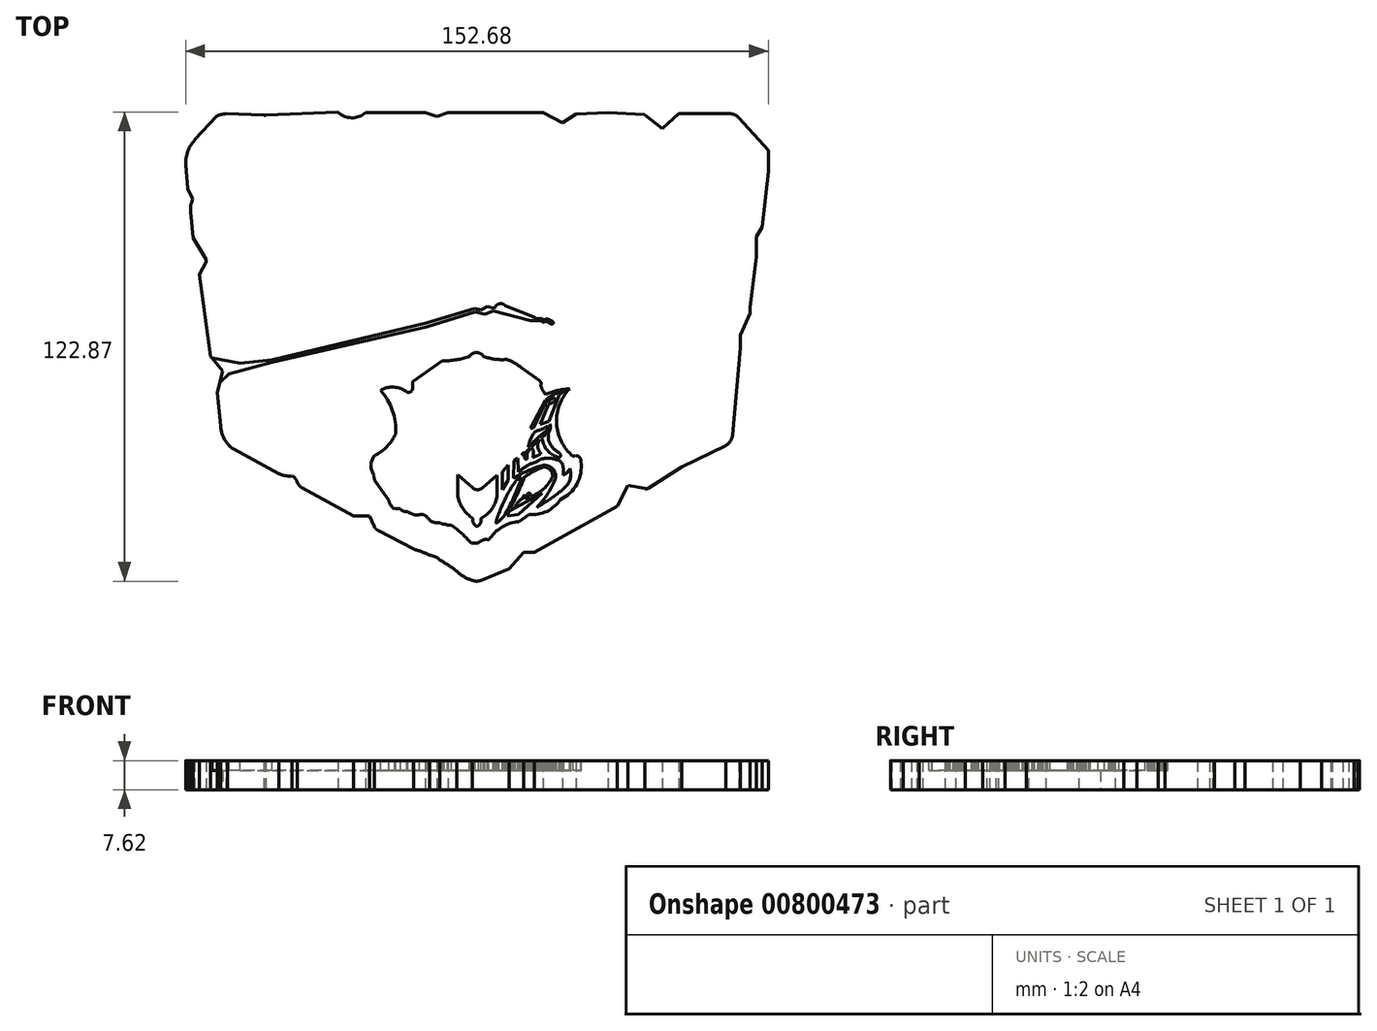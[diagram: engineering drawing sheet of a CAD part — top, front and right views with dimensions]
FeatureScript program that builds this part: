
annotation { "Feature Type Name" : "Feature", "Feature Type Description" : "" }
export const myFeature = defineFeature(function(context is Context, id is Id, definition is map)
    precondition{}
    {
        {
            var Q0;
            Q0=qCreatedBy(makeId("Top.planeOp"),FACE);
            var sketch = newSketch(context, id + "F0", { "sketchPlane" : qUnion([Q0])});
            skArc(sketch, "E0", {"start": v(-74.3, 49.3) * mm, "mid": v(-76.18, 45.63) * mm, "end": v(-76.24, 41.51) * mm});
            skArc(sketch, "E1", {"start": v(-74.3, 49.3) * mm, "mid": v(-74.1, 49.43) * mm, "end": v(-74.08, 49.68) * mm});
            skLineSegment(sketch, "E2", {"start": v(-74.08, 49.68) * mm, "end": v(-68.28, 55.88) * mm});
            skArc(sketch, "E3", {"start": v(-65.82, 56.46) * mm, "mid": v(-67.08, 56.27) * mm, "end": v(-68.28, 55.88) * mm});
            skLineSegment(sketch, "E4", {"start": v(-65.82, 56.46) * mm, "end": v(-55.9, 56.11) * mm});
            skArc(sketch, "E5", {"start": v(-55.83, 56.11) * mm, "mid": v(-55.67, 55.96) * mm, "end": v(-55.5, 56.11) * mm});
            skLineSegment(sketch, "E6", {"start": v(-55.5, 56.11) * mm, "end": v(-36.55, 56.87) * mm});
            skArc(sketch, "E7", {"start": v(-36.55, 56.87) * mm, "mid": v(-32.97, 55.4) * mm, "end": v(-29.34, 56.72) * mm});
            skLineSegment(sketch, "E8", {"start": v(-29.34, 56.72) * mm, "end": v(-13.61, 56.72) * mm});
            skLineSegment(sketch, "E9", {"start": v(-13.61, 56.72) * mm, "end": v(-10.61, 55.77) * mm});
            skLineSegment(sketch, "E10", {"start": v(-10.61, 55.77) * mm, "end": v(-7.76, 56.72) * mm});
            skLineSegment(sketch, "E11", {"start": v(-7.76, 56.72) * mm, "end": v(17.22, 56.72) * mm});
            skLineSegment(sketch, "E12", {"start": v(17.22, 56.72) * mm, "end": v(22.24, 54.04) * mm});
            skLineSegment(sketch, "E13", {"start": v(22.24, 54.04) * mm, "end": v(25.86, 56.34) * mm});
            skLineSegment(sketch, "E14", {"start": v(25.86, 56.34) * mm, "end": v(34.15, 56.72) * mm});
            skLineSegment(sketch, "E15", {"start": v(34.15, 56.72) * mm, "end": v(43.7, 56.3) * mm});
            skLineSegment(sketch, "E16", {"start": v(43.7, 56.3) * mm, "end": v(48.5, 52.57) * mm});
            skLineSegment(sketch, "E17", {"start": v(48.5, 52.57) * mm, "end": v(52.7, 56.5) * mm});
            skLineSegment(sketch, "E18", {"start": v(52.7, 56.5) * mm, "end": v(65.86, 56.5) * mm});
            skArc(sketch, "E19", {"start": v(68.51, 55.38) * mm, "mid": v(67.3, 56.2) * mm, "end": v(65.86, 56.5) * mm});
            skLineSegment(sketch, "E20", {"start": v(68.51, 55.38) * mm, "end": v(76.23, 46.9) * mm});
            skLineSegment(sketch, "E21", {"start": v(76.23, 46.9) * mm, "end": v(76.23, 41.38) * mm});
            skLineSegment(sketch, "E22", {"start": v(76.23, 41.38) * mm, "end": v(74.54, 26.82) * mm});
            skLineSegment(sketch, "E23", {"start": v(74.54, 26.82) * mm, "end": v(73.04, 24.23) * mm});
            skLineSegment(sketch, "E24", {"start": v(73.04, 24.23) * mm, "end": v(73.04, 18.9) * mm});
            skLineSegment(sketch, "E25", {"start": v(73.04, 18.9) * mm, "end": v(71.4, 5.86) * mm});
            skLineSegment(sketch, "E26", {"start": v(71.4, 5.86) * mm, "end": v(71.4, 4.2) * mm});
            skLineSegment(sketch, "E27", {"start": v(71.4, 4.2) * mm, "end": v(68.93, -1.48) * mm});
            skLineSegment(sketch, "E28", {"start": v(68.93, -1.48) * mm, "end": v(68.93, -4.86) * mm});
            skLineSegment(sketch, "E29", {"start": v(68.93, -4.86) * mm, "end": v(66.82, -27.75) * mm});
            skArc(sketch, "E30", {"start": v(65.02, -30.47) * mm, "mid": v(66.26, -29.34) * mm, "end": v(66.82, -27.75) * mm});
            skLineSegment(sketch, "E31", {"start": v(65.02, -30.47) * mm, "end": v(53.53, -36.04) * mm});
            skLineSegment(sketch, "E32", {"start": v(53.53, -36.04) * mm, "end": v(44.7, -41.7) * mm});
            skArc(sketch, "E33", {"start": v(43.82, -41.7) * mm, "mid": v(44.26, -41.84) * mm, "end": v(44.7, -41.7) * mm});
            skLineSegment(sketch, "E34", {"start": v(43.82, -41.7) * mm, "end": v(39.36, -40.85) * mm});
            skLineSegment(sketch, "E35", {"start": v(39.36, -40.85) * mm, "end": v(36.62, -46.35) * mm});
            skLineSegment(sketch, "E36", {"start": v(36.62, -46.35) * mm, "end": v(14.92, -58.42) * mm});
            skLineSegment(sketch, "E37", {"start": v(14.92, -58.42) * mm, "end": v(12.09, -58.42) * mm});
            skLineSegment(sketch, "E38", {"start": v(12.09, -58.42) * mm, "end": v(8.29, -62.7) * mm});
            skLineSegment(sketch, "E39", {"start": v(8.29, -62.7) * mm, "end": v(0.97, -65.76) * mm});
            skArc(sketch, "E40", {"start": v(-1.37, -65.76) * mm, "mid": v(-0.2, -66) * mm, "end": v(0.97, -65.76) * mm});
            skArc(sketch, "E41", {"start": v(-5.4, -63.42) * mm, "mid": v(-3.54, -64.85) * mm, "end": v(-1.37, -65.76) * mm});
            skArc(sketch, "E42", {"start": v(-5.4, -63.42) * mm, "mid": v(-7.55, -61.84) * mm, "end": v(-9.83, -60.45) * mm});
            skArc(sketch, "E43", {"start": v(-9.83, -60.45) * mm, "mid": v(-11.07, -59.62) * mm, "end": v(-12.5, -59.18) * mm});
            skArc(sketch, "E44", {"start": v(-12.5, -59.18) * mm, "mid": v(-14.57, -58.3) * mm, "end": v(-16.7, -57.58) * mm});
            skLineSegment(sketch, "E45", {"start": v(-16.7, -57.58) * mm, "end": v(-26, -52.75) * mm});
            skArc(sketch, "E46", {"start": v(-27.04, -51.75) * mm, "mid": v(-26.6, -52.33) * mm, "end": v(-26, -52.75) * mm});
            skLineSegment(sketch, "E47", {"start": v(-27.04, -51.75) * mm, "end": v(-28.26, -48.93) * mm});
            skLineSegment(sketch, "E48", {"start": v(-28.26, -48.93) * mm, "end": v(-32.5, -48.93) * mm});
            skLineSegment(sketch, "E49", {"start": v(-32.5, -48.93) * mm, "end": v(-45.88, -41.56) * mm});
            skArc(sketch, "E50", {"start": v(-47.22, -40.08) * mm, "mid": v(-46.67, -40.93) * mm, "end": v(-45.88, -41.56) * mm});
            skArc(sketch, "E51", {"start": v(-47.22, -40.08) * mm, "mid": v(-47.7, -39.1) * mm, "end": v(-48.54, -38.41) * mm});
            skArc(sketch, "E52", {"start": v(-52.05, -37.8) * mm, "mid": v(-50.34, -38.37) * mm, "end": v(-48.54, -38.41) * mm});
            skLineSegment(sketch, "E53", {"start": v(-52.05, -37.8) * mm, "end": v(-63.85, -31.42) * mm});
            skArc(sketch, "E54", {"start": v(-65.42, -29.96) * mm, "mid": v(-64.73, -30.8) * mm, "end": v(-63.85, -31.42) * mm});
            skArc(sketch, "E55", {"start": v(-67.28, -25.3) * mm, "mid": v(-66.76, -27.79) * mm, "end": v(-65.42, -29.96) * mm});
            skLineSegment(sketch, "E56", {"start": v(-67.28, -25.3) * mm, "end": v(-68.16, -16.7) * mm});
            skLineSegment(sketch, "E57", {"start": v(-68.16, -16.7) * mm, "end": v(-66.77, -10.96) * mm});
            skLineSegment(sketch, "E58", {"start": v(-66.77, -10.96) * mm, "end": v(-69.9, -7.14) * mm});
            skLineSegment(sketch, "E59", {"start": v(-69.9, -7.14) * mm, "end": v(-72.82, 14.38) * mm});
            skLineSegment(sketch, "E60", {"start": v(-72.82, 14.38) * mm, "end": v(-71.12, 17.62) * mm});
            skLineSegment(sketch, "E61", {"start": v(-71.12, 17.62) * mm, "end": v(-71.12, 18.31) * mm});
            skLineSegment(sketch, "E62", {"start": v(-71.12, 18.31) * mm, "end": v(-74.46, 23.95) * mm});
            skLineSegment(sketch, "E63", {"start": v(-74.46, 23.95) * mm, "end": v(-75.16, 30.76) * mm});
            skArc(sketch, "E64", {"start": v(-74.93, 33.15) * mm, "mid": v(-75.16, 31.97) * mm, "end": v(-75.16, 30.76) * mm});
            skLineSegment(sketch, "E65", {"start": v(-74.93, 33.15) * mm, "end": v(-74.62, 34.16) * mm});
            skLineSegment(sketch, "E66", {"start": v(-74.62, 34.16) * mm, "end": v(-75.9, 36.77) * mm});
            skLineSegment(sketch, "E67", {"start": v(-75.9, 36.77) * mm, "end": v(-76.24, 41.51) * mm});
            skLineSegment(sketch, "E68", {"start": v(-55.9, 56.11) * mm, "end": v(-55.83, 56.11) * mm});
            skSolve(sketch);
        }
        {
            var Q0;
            Q0 = qSketchRegion(id + "F0", true);
            extrude(context, id + "F1", {"entities" : qUnion([Q0]), "depth" : 7.62 * mm, "offsetDistance" : 25.4 * mm});
        }
        {
            var Q0;
            Q0=makeQuery(id+"F1.opExtrude","CAP_FACE",FACE,{"disambiguationData":[OSD([sQuery(id+"F0.wireOp",EDGE,"E0"),sQuery(id+"F0.wireOp",EDGE,"E1"),sQuery(id+"F0.wireOp",EDGE,"E2"),sQuery(id+"F0.wireOp",EDGE,"E3"),sQuery(id+"F0.wireOp",EDGE,"E4"),sQuery(id+"F0.wireOp",EDGE,"E5"),sQuery(id+"F0.wireOp",EDGE,"E6"),sQuery(id+"F0.wireOp",EDGE,"E7"),sQuery(id+"F0.wireOp",EDGE,"E8"),sQuery(id+"F0.wireOp",EDGE,"E9"),sQuery(id+"F0.wireOp",EDGE,"E10"),sQuery(id+"F0.wireOp",EDGE,"E11"),sQuery(id+"F0.wireOp",EDGE,"E12"),sQuery(id+"F0.wireOp",EDGE,"E13"),sQuery(id+"F0.wireOp",EDGE,"E14"),sQuery(id+"F0.wireOp",EDGE,"E15"),sQuery(id+"F0.wireOp",EDGE,"E16"),sQuery(id+"F0.wireOp",EDGE,"E17"),sQuery(id+"F0.wireOp",EDGE,"E18"),sQuery(id+"F0.wireOp",EDGE,"E19"),sQuery(id+"F0.wireOp",EDGE,"E20"),sQuery(id+"F0.wireOp",EDGE,"E21"),sQuery(id+"F0.wireOp",EDGE,"E22"),sQuery(id+"F0.wireOp",EDGE,"E23"),sQuery(id+"F0.wireOp",EDGE,"E24"),sQuery(id+"F0.wireOp",EDGE,"E25"),sQuery(id+"F0.wireOp",EDGE,"E26"),sQuery(id+"F0.wireOp",EDGE,"E27"),sQuery(id+"F0.wireOp",EDGE,"E28"),sQuery(id+"F0.wireOp",EDGE,"E29"),sQuery(id+"F0.wireOp",EDGE,"E30"),sQuery(id+"F0.wireOp",EDGE,"E31"),sQuery(id+"F0.wireOp",EDGE,"E32"),sQuery(id+"F0.wireOp",EDGE,"E33"),sQuery(id+"F0.wireOp",EDGE,"E34"),sQuery(id+"F0.wireOp",EDGE,"E35"),sQuery(id+"F0.wireOp",EDGE,"E36"),sQuery(id+"F0.wireOp",EDGE,"E37"),sQuery(id+"F0.wireOp",EDGE,"E38"),sQuery(id+"F0.wireOp",EDGE,"E39"),sQuery(id+"F0.wireOp",EDGE,"E40"),sQuery(id+"F0.wireOp",EDGE,"E41"),sQuery(id+"F0.wireOp",EDGE,"E42"),sQuery(id+"F0.wireOp",EDGE,"E43"),sQuery(id+"F0.wireOp",EDGE,"E44"),sQuery(id+"F0.wireOp",EDGE,"E45"),sQuery(id+"F0.wireOp",EDGE,"E46"),sQuery(id+"F0.wireOp",EDGE,"E47"),sQuery(id+"F0.wireOp",EDGE,"E48"),sQuery(id+"F0.wireOp",EDGE,"E49"),sQuery(id+"F0.wireOp",EDGE,"E50"),sQuery(id+"F0.wireOp",EDGE,"E51"),sQuery(id+"F0.wireOp",EDGE,"E52"),sQuery(id+"F0.wireOp",EDGE,"E53"),sQuery(id+"F0.wireOp",EDGE,"E54"),sQuery(id+"F0.wireOp",EDGE,"E55"),sQuery(id+"F0.wireOp",EDGE,"E56"),sQuery(id+"F0.wireOp",EDGE,"E57"),sQuery(id+"F0.wireOp",EDGE,"E58"),sQuery(id+"F0.wireOp",EDGE,"E59"),sQuery(id+"F0.wireOp",EDGE,"E60"),sQuery(id+"F0.wireOp",EDGE,"E61"),sQuery(id+"F0.wireOp",EDGE,"E62"),sQuery(id+"F0.wireOp",EDGE,"E63"),sQuery(id+"F0.wireOp",EDGE,"E64"),sQuery(id+"F0.wireOp",EDGE,"E65"),sQuery(id+"F0.wireOp",EDGE,"E66"),sQuery(id+"F0.wireOp",EDGE,"E67"),sQuery(id+"F0.wireOp",EDGE,"E68")])],"isStart":false});
            var sketch = newSketch(context, id + "F2", { "sketchPlane" : qUnion([Q0])});
            skLineSegment(sketch, "E69", {"start": v(-62.2, -8.88) * mm, "end": v(-53.85, -8.03) * mm});
            skLineSegment(sketch, "E70", {"start": v(-53.85, -8.03) * mm, "end": v(-53.79, -8.6) * mm});
            skLineSegment(sketch, "E71", {"start": v(-53.79, -8.6) * mm, "end": v(-65.1, -11.64) * mm});
            skLineSegment(sketch, "E72", {"start": v(-62.2, -8.88) * mm, "end": v(-69.59, -7.53) * mm});
            skLineSegment(sketch, "E73", {"start": v(-69.59, -7.53) * mm, "end": v(-66.77, -10.96) * mm});
            skLineSegment(sketch, "E74", {"start": v(-66.77, -10.96) * mm, "end": v(-67.5, -14) * mm});
            skLineSegment(sketch, "E75", {"start": v(-67.5, -14) * mm, "end": v(-65.1, -11.64) * mm});
            skSolve(sketch);
        }
        {
            var Q0;
            Q0 = qSketchRegion(id + "F2", true);
            extrude(context, id + "F3", {"entities" : qUnion([Q0]), "operationType" : NewBodyOperationType.REMOVE, "oppositeDirection" : true, "depth" : 2.54 * mm, "offsetDistance" : 25.4 * mm});
        }
        {
            var Q0;
            Q0=makeQuery(id+"F1.opExtrude","CAP_FACE",FACE,{"disambiguationData":[OSD([sQuery(id+"F0.wireOp",EDGE,"E0"),sQuery(id+"F0.wireOp",EDGE,"E1"),sQuery(id+"F0.wireOp",EDGE,"E2"),sQuery(id+"F0.wireOp",EDGE,"E3"),sQuery(id+"F0.wireOp",EDGE,"E4"),sQuery(id+"F0.wireOp",EDGE,"E5"),sQuery(id+"F0.wireOp",EDGE,"E6"),sQuery(id+"F0.wireOp",EDGE,"E7"),sQuery(id+"F0.wireOp",EDGE,"E8"),sQuery(id+"F0.wireOp",EDGE,"E9"),sQuery(id+"F0.wireOp",EDGE,"E10"),sQuery(id+"F0.wireOp",EDGE,"E11"),sQuery(id+"F0.wireOp",EDGE,"E12"),sQuery(id+"F0.wireOp",EDGE,"E13"),sQuery(id+"F0.wireOp",EDGE,"E14"),sQuery(id+"F0.wireOp",EDGE,"E15"),sQuery(id+"F0.wireOp",EDGE,"E16"),sQuery(id+"F0.wireOp",EDGE,"E17"),sQuery(id+"F0.wireOp",EDGE,"E18"),sQuery(id+"F0.wireOp",EDGE,"E19"),sQuery(id+"F0.wireOp",EDGE,"E20"),sQuery(id+"F0.wireOp",EDGE,"E21"),sQuery(id+"F0.wireOp",EDGE,"E22"),sQuery(id+"F0.wireOp",EDGE,"E23"),sQuery(id+"F0.wireOp",EDGE,"E24"),sQuery(id+"F0.wireOp",EDGE,"E25"),sQuery(id+"F0.wireOp",EDGE,"E26"),sQuery(id+"F0.wireOp",EDGE,"E27"),sQuery(id+"F0.wireOp",EDGE,"E28"),sQuery(id+"F0.wireOp",EDGE,"E29"),sQuery(id+"F0.wireOp",EDGE,"E30"),sQuery(id+"F0.wireOp",EDGE,"E31"),sQuery(id+"F0.wireOp",EDGE,"E32"),sQuery(id+"F0.wireOp",EDGE,"E33"),sQuery(id+"F0.wireOp",EDGE,"E34"),sQuery(id+"F0.wireOp",EDGE,"E35"),sQuery(id+"F0.wireOp",EDGE,"E36"),sQuery(id+"F0.wireOp",EDGE,"E37"),sQuery(id+"F0.wireOp",EDGE,"E38"),sQuery(id+"F0.wireOp",EDGE,"E39"),sQuery(id+"F0.wireOp",EDGE,"E40"),sQuery(id+"F0.wireOp",EDGE,"E41"),sQuery(id+"F0.wireOp",EDGE,"E42"),sQuery(id+"F0.wireOp",EDGE,"E43"),sQuery(id+"F0.wireOp",EDGE,"E44"),sQuery(id+"F0.wireOp",EDGE,"E45"),sQuery(id+"F0.wireOp",EDGE,"E46"),sQuery(id+"F0.wireOp",EDGE,"E47"),sQuery(id+"F0.wireOp",EDGE,"E48"),sQuery(id+"F0.wireOp",EDGE,"E49"),sQuery(id+"F0.wireOp",EDGE,"E50"),sQuery(id+"F0.wireOp",EDGE,"E51"),sQuery(id+"F0.wireOp",EDGE,"E52"),sQuery(id+"F0.wireOp",EDGE,"E53"),sQuery(id+"F0.wireOp",EDGE,"E54"),sQuery(id+"F0.wireOp",EDGE,"E55"),sQuery(id+"F0.wireOp",EDGE,"E56"),sQuery(id+"F0.wireOp",EDGE,"E57"),sQuery(id+"F0.wireOp",EDGE,"E58"),sQuery(id+"F0.wireOp",EDGE,"E59"),sQuery(id+"F0.wireOp",EDGE,"E60"),sQuery(id+"F0.wireOp",EDGE,"E61"),sQuery(id+"F0.wireOp",EDGE,"E62"),sQuery(id+"F0.wireOp",EDGE,"E63"),sQuery(id+"F0.wireOp",EDGE,"E64"),sQuery(id+"F0.wireOp",EDGE,"E65"),sQuery(id+"F0.wireOp",EDGE,"E66"),sQuery(id+"F0.wireOp",EDGE,"E67"),sQuery(id+"F0.wireOp",EDGE,"E68")])],"isStart":false});
            var sketch = newSketch(context, id + "F4", { "sketchPlane" : qUnion([Q0])});
            skLineSegment(sketch, "E76", {"start": v(-53.85, -8.03) * mm, "end": v(-13.44, 1.68) * mm});
            skLineSegment(sketch, "E77", {"start": v(-13.44, 1.68) * mm, "end": v(-0.77, 5.43) * mm});
            skLineSegment(sketch, "E78", {"start": v(-0.77, 5.43) * mm, "end": v(1, 5.12) * mm});
            skLineSegment(sketch, "E79", {"start": v(1, 5.12) * mm, "end": v(2.62, 6) * mm});
            skLineSegment(sketch, "E80", {"start": v(2.62, 6) * mm, "end": v(4.52, 5.5) * mm});
            skArc(sketch, "E81", {"start": v(7.22, 6.24) * mm, "mid": v(5.66, 6.65) * mm, "end": v(4.52, 5.5) * mm});
            skLineSegment(sketch, "E82", {"start": v(7.22, 6.24) * mm, "end": v(14.94, 3.2) * mm});
            skLineSegment(sketch, "E83", {"start": v(14.94, 3.2) * mm, "end": v(15.44, 2.8) * mm});
            skLineSegment(sketch, "E84", {"start": v(15.44, 2.8) * mm, "end": v(16.91, 2.8) * mm});
            skLineSegment(sketch, "E85", {"start": v(16.91, 2.8) * mm, "end": v(17.41, 2.42) * mm});
            skLineSegment(sketch, "E86", {"start": v(17.41, 2.42) * mm, "end": v(18.22, 2.8) * mm});
            skLineSegment(sketch, "E87", {"start": v(18.22, 2.8) * mm, "end": v(19.73, 2) * mm});
            skArc(sketch, "E88", {"start": v(19.37, 1.44) * mm, "mid": v(19.85, 1.52) * mm, "end": v(19.73, 2) * mm});
            skLineSegment(sketch, "E89", {"start": v(19.37, 1.44) * mm, "end": v(18, 2.12) * mm});
            skLineSegment(sketch, "E90", {"start": v(18, 2.12) * mm, "end": v(17.5, 1.76) * mm});
            skLineSegment(sketch, "E91", {"start": v(17.5, 1.76) * mm, "end": v(16.58, 2.23) * mm});
            skLineSegment(sketch, "E92", {"start": v(16.58, 2.23) * mm, "end": v(13.9, 2.23) * mm});
            skLineSegment(sketch, "E93", {"start": v(13.9, 2.23) * mm, "end": v(4.1, 4.76) * mm});
            skLineSegment(sketch, "E94", {"start": v(4.1, 4.76) * mm, "end": v(1.94, 3.91) * mm});
            skLineSegment(sketch, "E95", {"start": v(1.94, 3.91) * mm, "end": v(-0.6, 4.57) * mm});
            skLineSegment(sketch, "E96", {"start": v(-0.6, 4.57) * mm, "end": v(-13.3, 0.64) * mm});
            skLineSegment(sketch, "E97", {"start": v(-13.3, 0.64) * mm, "end": v(-53.79, -8.6) * mm});
            skLineSegment(sketch, "E98", {"start": v(-53.79, -8.6) * mm, "end": v(-53.85, -8.03) * mm});
            skSolve(sketch);
        }
        {
            var Q0;
            Q0 = qSketchRegion(id + "F4", true);
            extrude(context, id + "F5", {"entities" : qUnion([Q0]), "operationType" : NewBodyOperationType.REMOVE, "oppositeDirection" : true, "depth" : 2.54 * mm, "offsetDistance" : 25.4 * mm});
        }
        {
            var Q0;
            Q0=makeQuery(id+"F1.opExtrude","CAP_FACE",FACE,{"disambiguationData":[OSD([sQuery(id+"F0.wireOp",EDGE,"E0"),sQuery(id+"F0.wireOp",EDGE,"E1"),sQuery(id+"F0.wireOp",EDGE,"E2"),sQuery(id+"F0.wireOp",EDGE,"E3"),sQuery(id+"F0.wireOp",EDGE,"E4"),sQuery(id+"F0.wireOp",EDGE,"E5"),sQuery(id+"F0.wireOp",EDGE,"E6"),sQuery(id+"F0.wireOp",EDGE,"E7"),sQuery(id+"F0.wireOp",EDGE,"E8"),sQuery(id+"F0.wireOp",EDGE,"E9"),sQuery(id+"F0.wireOp",EDGE,"E10"),sQuery(id+"F0.wireOp",EDGE,"E11"),sQuery(id+"F0.wireOp",EDGE,"E12"),sQuery(id+"F0.wireOp",EDGE,"E13"),sQuery(id+"F0.wireOp",EDGE,"E14"),sQuery(id+"F0.wireOp",EDGE,"E15"),sQuery(id+"F0.wireOp",EDGE,"E16"),sQuery(id+"F0.wireOp",EDGE,"E17"),sQuery(id+"F0.wireOp",EDGE,"E18"),sQuery(id+"F0.wireOp",EDGE,"E19"),sQuery(id+"F0.wireOp",EDGE,"E20"),sQuery(id+"F0.wireOp",EDGE,"E21"),sQuery(id+"F0.wireOp",EDGE,"E22"),sQuery(id+"F0.wireOp",EDGE,"E23"),sQuery(id+"F0.wireOp",EDGE,"E24"),sQuery(id+"F0.wireOp",EDGE,"E25"),sQuery(id+"F0.wireOp",EDGE,"E26"),sQuery(id+"F0.wireOp",EDGE,"E27"),sQuery(id+"F0.wireOp",EDGE,"E28"),sQuery(id+"F0.wireOp",EDGE,"E29"),sQuery(id+"F0.wireOp",EDGE,"E30"),sQuery(id+"F0.wireOp",EDGE,"E31"),sQuery(id+"F0.wireOp",EDGE,"E32"),sQuery(id+"F0.wireOp",EDGE,"E33"),sQuery(id+"F0.wireOp",EDGE,"E34"),sQuery(id+"F0.wireOp",EDGE,"E35"),sQuery(id+"F0.wireOp",EDGE,"E36"),sQuery(id+"F0.wireOp",EDGE,"E37"),sQuery(id+"F0.wireOp",EDGE,"E38"),sQuery(id+"F0.wireOp",EDGE,"E39"),sQuery(id+"F0.wireOp",EDGE,"E40"),sQuery(id+"F0.wireOp",EDGE,"E41"),sQuery(id+"F0.wireOp",EDGE,"E42"),sQuery(id+"F0.wireOp",EDGE,"E43"),sQuery(id+"F0.wireOp",EDGE,"E44"),sQuery(id+"F0.wireOp",EDGE,"E45"),sQuery(id+"F0.wireOp",EDGE,"E46"),sQuery(id+"F0.wireOp",EDGE,"E47"),sQuery(id+"F0.wireOp",EDGE,"E48"),sQuery(id+"F0.wireOp",EDGE,"E49"),sQuery(id+"F0.wireOp",EDGE,"E50"),sQuery(id+"F0.wireOp",EDGE,"E51"),sQuery(id+"F0.wireOp",EDGE,"E52"),sQuery(id+"F0.wireOp",EDGE,"E53"),sQuery(id+"F0.wireOp",EDGE,"E54"),sQuery(id+"F0.wireOp",EDGE,"E55"),sQuery(id+"F0.wireOp",EDGE,"E56"),sQuery(id+"F0.wireOp",EDGE,"E57"),sQuery(id+"F0.wireOp",EDGE,"E58"),sQuery(id+"F0.wireOp",EDGE,"E59"),sQuery(id+"F0.wireOp",EDGE,"E60"),sQuery(id+"F0.wireOp",EDGE,"E61"),sQuery(id+"F0.wireOp",EDGE,"E62"),sQuery(id+"F0.wireOp",EDGE,"E63"),sQuery(id+"F0.wireOp",EDGE,"E64"),sQuery(id+"F0.wireOp",EDGE,"E65"),sQuery(id+"F0.wireOp",EDGE,"E66"),sQuery(id+"F0.wireOp",EDGE,"E67"),sQuery(id+"F0.wireOp",EDGE,"E68")])],"isStart":false});
            var sketch = newSketch(context, id + "F6", { "sketchPlane" : qUnion([Q0])});
            skArc(sketch, "E99", {"start": v(-20.11, -47.13) * mm, "mid": v(-19.28, -47.7) * mm, "end": v(-18.27, -47.7) * mm});
            skArc(sketch, "E100", {"start": v(-20.11, -47.13) * mm, "mid": v(-20.9, -46.94) * mm, "end": v(-21.7, -47.13) * mm});
            skArc(sketch, "E101", {"start": v(-23.24, -44.79) * mm, "mid": v(-22.7, -46.1) * mm, "end": v(-21.7, -47.13) * mm});
            skLineSegment(sketch, "E102", {"start": v(-23.24, -44.79) * mm, "end": v(-26.63, -40.04) * mm});
            skArc(sketch, "E103", {"start": v(-27.06, -38.27) * mm, "mid": v(-27.02, -39.2) * mm, "end": v(-26.63, -40.04) * mm});
            skArc(sketch, "E104", {"start": v(-27.06, -33.17) * mm, "mid": v(-27.9, -35.72) * mm, "end": v(-27.06, -38.27) * mm});
            skArc(sketch, "E105", {"start": v(-27.06, -33.17) * mm, "mid": v(-23.74, -30.77) * mm, "end": v(-21.42, -27.4) * mm});
            skArc(sketch, "E106", {"start": v(-21.42, -27.4) * mm, "mid": v(-22.29, -21.3) * mm, "end": v(-25.38, -16) * mm});
            skArc(sketch, "E107", {"start": v(-18.55, -16.41) * mm, "mid": v(-21.9, -15.16) * mm, "end": v(-25.38, -16) * mm});
            skArc(sketch, "E108", {"start": v(-18.55, -16.41) * mm, "mid": v(-17.56, -16.41) * mm, "end": v(-17, -15.6) * mm});
            skLineSegment(sketch, "E109", {"start": v(-17, -15.6) * mm, "end": v(-17, -13.67) * mm});
            skLineSegment(sketch, "E110", {"start": v(-17, -13.67) * mm, "end": v(-9.19, -8.3) * mm});
            skArc(sketch, "E111", {"start": v(-9.19, -8.3) * mm, "mid": v(-5.58, -8) * mm, "end": v(-2.08, -7.11) * mm});
            skArc(sketch, "E112", {"start": v(1.59, -7.11) * mm, "mid": v(-0.25, -6.1) * mm, "end": v(-2.08, -7.11) * mm});
            skArc(sketch, "E113", {"start": v(1.59, -7.11) * mm, "mid": v(4.56, -7.83) * mm, "end": v(7.61, -7.92) * mm});
            skArc(sketch, "E114", {"start": v(11.42, -10.02) * mm, "mid": v(9.62, -8.78) * mm, "end": v(7.61, -7.92) * mm});
            skLineSegment(sketch, "E115", {"start": v(11.42, -10.02) * mm, "end": v(16.29, -13.51) * mm});
            skArc(sketch, "E116", {"start": v(16.59, -14.64) * mm, "mid": v(16.64, -14.02) * mm, "end": v(16.29, -13.51) * mm});
            skArc(sketch, "E117", {"start": v(16.59, -14.64) * mm, "mid": v(17.06, -15.93) * mm, "end": v(17.85, -17.06) * mm});
            skArc(sketch, "E118", {"start": v(24.16, -15.59) * mm, "mid": v(20.94, -16.05) * mm, "end": v(17.85, -17.06) * mm});
            skArc(sketch, "E119", {"start": v(24.16, -15.59) * mm, "mid": v(20.72, -24.64) * mm, "end": v(25.08, -33.28) * mm});
            skArc(sketch, "E120", {"start": v(27.1, -34.69) * mm, "mid": v(26.54, -33.34) * mm, "end": v(25.08, -33.28) * mm});
            skArc(sketch, "E121", {"start": v(21.7, -44.61) * mm, "mid": v(26.07, -40.55) * mm, "end": v(27.1, -34.69) * mm});
            skArc(sketch, "E122", {"start": v(13.5, -48.5) * mm, "mid": v(18.15, -47.72) * mm, "end": v(21.7, -44.61) * mm});
            skLineSegment(sketch, "E123", {"start": v(13.5, -48.5) * mm, "end": v(10.87, -50.4) * mm});
            skArc(sketch, "E124", {"start": v(10.87, -50.4) * mm, "mid": v(6.37, -51.86) * mm, "end": v(2.99, -55.17) * mm});
            skArc(sketch, "E125", {"start": v(2.99, -55.17) * mm, "mid": v(1.54, -55.15) * mm, "end": v(0.32, -55.95) * mm});
            skArc(sketch, "E126", {"start": v(-1.72, -55.95) * mm, "mid": v(-0.7, -56) * mm, "end": v(0.32, -55.95) * mm});
            skArc(sketch, "E127", {"start": v(-1.72, -55.95) * mm, "mid": v(-4.13, -53.5) * mm, "end": v(-6.82, -51.35) * mm});
            skLineSegment(sketch, "E128", {"start": v(-6.82, -51.35) * mm, "end": v(-7.86, -51.35) * mm});
            skArc(sketch, "E129", {"start": v(-7.86, -51.35) * mm, "mid": v(-8.22, -51.12) * mm, "end": v(-8.65, -51.09) * mm});
            skArc(sketch, "E130", {"start": v(-9.94, -50.62) * mm, "mid": v(-9.32, -50.93) * mm, "end": v(-8.65, -51.09) * mm});
            skArc(sketch, "E131", {"start": v(-18.27, -47.7) * mm, "mid": v(-16.82, -48.52) * mm, "end": v(-15.15, -48.58) * mm});
            skArc(sketch, "E132", {"start": v(-13.1, -49.3) * mm, "mid": v(-14.02, -48.63) * mm, "end": v(-15.15, -48.58) * mm});
            skArc(sketch, "E133", {"start": v(-13.1, -49.3) * mm, "mid": v(-11.74, -50.47) * mm, "end": v(-9.94, -50.62) * mm});
            skPoint(sketch, "E134.endSnap0", {"position": v(0.1, -42.1) * mm});
            skLineSegment(sketch, "E135", {"start": v(-5.2, -38.16) * mm, "end": v(-1.24, -41.57) * mm});
            skArc(sketch, "E136", {"start": v(-1.24, -41.57) * mm, "mid": v(0.02, -42.04) * mm, "end": v(1.28, -41.57) * mm});
            skLineSegment(sketch, "E137", {"start": v(1.28, -41.57) * mm, "end": v(5.12, -38.26) * mm});
            skLineSegment(sketch, "E138", {"start": v(5.12, -38.26) * mm, "end": v(5.12, -43.83) * mm});
            skArc(sketch, "E139", {"start": v(-0.58, -51.38) * mm, "mid": v(-0.1, -51.6) * mm, "end": v(0.36, -51.38) * mm});
            skArc(sketch, "E140", {"start": v(-1.24, -49.54) * mm, "mid": v(-1.13, -50.54) * mm, "end": v(-0.58, -51.38) * mm});
            skLineSegment(sketch, "E141", {"start": v(-5.2, -38.16) * mm, "end": v(-5.2, -43.83) * mm});
            skArc(sketch, "E142", {"start": v(-5.2, -43.83) * mm, "mid": v(-3.75, -47.05) * mm, "end": v(-1.24, -49.54) * mm});
            skArc(sketch, "E143", {"start": v(0.36, -51.38) * mm, "mid": v(0.89, -50.53) * mm, "end": v(0.95, -49.54) * mm});
            skArc(sketch, "E144", {"start": v(0.95, -49.54) * mm, "mid": v(3.71, -47.18) * mm, "end": v(5.12, -43.83) * mm});
            skArc(sketch, "E145", {"start": v(10.93, -39.07) * mm, "mid": v(10.4, -39.4) * mm, "end": v(9.97, -39.83) * mm});
            skArc(sketch, "E146", {"start": v(11.48, -39.29) * mm, "mid": v(11.3, -38.93) * mm, "end": v(10.93, -39.07) * mm});
            skArc(sketch, "E147", {"start": v(7, -48.92) * mm, "mid": v(9.46, -44.2) * mm, "end": v(11.48, -39.29) * mm});
            skArc(sketch, "E148", {"start": v(4.87, -50.86) * mm, "mid": v(6, -49.96) * mm, "end": v(7, -48.92) * mm});
            skArc(sketch, "E149", {"start": v(5.66, -48.21) * mm, "mid": v(5.15, -49.5) * mm, "end": v(4.87, -50.86) * mm});
            skArc(sketch, "E150", {"start": v(9.97, -39.83) * mm, "mid": v(7.55, -43.89) * mm, "end": v(5.66, -48.21) * mm});
            skLineSegment(sketch, "E151", {"start": v(6.5, -37.37) * mm, "end": v(8.1, -35.62) * mm});
            skLineSegment(sketch, "E152", {"start": v(8.1, -35.62) * mm, "end": v(8.1, -39.51) * mm});
            skLineSegment(sketch, "E153", {"start": v(8.1, -39.51) * mm, "end": v(6.56, -42.01) * mm});
            skLineSegment(sketch, "E154", {"start": v(6.56, -42.01) * mm, "end": v(6.5, -37.37) * mm});
            skLineSegment(sketch, "E155", {"start": v(9.62, -34.38) * mm, "end": v(10.66, -33.8) * mm});
            skLineSegment(sketch, "E156", {"start": v(10.66, -33.8) * mm, "end": v(10.75, -37.37) * mm});
            skArc(sketch, "E157", {"start": v(13.97, -35.23) * mm, "mid": v(12.32, -36.24) * mm, "end": v(10.75, -37.37) * mm});
            skArc(sketch, "E158", {"start": v(13.97, -35.23) * mm, "mid": v(15.34, -34.75) * mm, "end": v(16.6, -34.01) * mm});
            skArc(sketch, "E159", {"start": v(21.94, -34.68) * mm, "mid": v(19.34, -33.82) * mm, "end": v(16.6, -34.01) * mm});
            skArc(sketch, "E160", {"start": v(22.46, -38.2) * mm, "mid": v(22.5, -36.4) * mm, "end": v(21.94, -34.68) * mm});
            skArc(sketch, "E161", {"start": v(22.46, -38.2) * mm, "mid": v(23.52, -37.51) * mm, "end": v(24.18, -36.43) * mm});
            skArc(sketch, "E162", {"start": v(22.69, -41.68) * mm, "mid": v(24.26, -39.29) * mm, "end": v(24.18, -36.43) * mm});
            skArc(sketch, "E163", {"start": v(15.5, -46.69) * mm, "mid": v(19.2, -44.35) * mm, "end": v(22.69, -41.68) * mm});
            skArc(sketch, "E164", {"start": v(15.5, -46.69) * mm, "mid": v(18.49, -43) * mm, "end": v(20.55, -38.72) * mm});
            skArc(sketch, "E165", {"start": v(20.55, -38.72) * mm, "mid": v(19.52, -36.36) * mm, "end": v(17.04, -35.67) * mm});
            skArc(sketch, "E166", {"start": v(17.04, -35.67) * mm, "mid": v(13.17, -37.08) * mm, "end": v(9.5, -38.97) * mm});
            skLineSegment(sketch, "E167", {"start": v(9.5, -38.97) * mm, "end": v(9.62, -34.38) * mm});
            skArc(sketch, "E168", {"start": v(12.55, -32.4) * mm, "mid": v(12.18, -32.42) * mm, "end": v(11.81, -32.49) * mm});
            skArc(sketch, "E169", {"start": v(13.56, -31.32) * mm, "mid": v(13, -31.82) * mm, "end": v(12.55, -32.4) * mm});
            skArc(sketch, "E170", {"start": v(13.7, -31.45) * mm, "mid": v(13.69, -31.32) * mm, "end": v(13.56, -31.32) * mm});
            skArc(sketch, "E171", {"start": v(12.99, -32.5) * mm, "mid": v(13.37, -32) * mm, "end": v(13.7, -31.45) * mm});
            skArc(sketch, "E172", {"start": v(12.99, -33.77) * mm, "mid": v(13.02, -33.13) * mm, "end": v(12.99, -32.5) * mm});
            skArc(sketch, "E173", {"start": v(12.41, -33.77) * mm, "mid": v(12.7, -34.05) * mm, "end": v(12.99, -33.77) * mm});
            skArc(sketch, "E174", {"start": v(12.41, -32.85) * mm, "mid": v(12.4, -33.3) * mm, "end": v(12.41, -33.77) * mm});
            skArc(sketch, "E175", {"start": v(11.8, -32.85) * mm, "mid": v(12.1, -32.9) * mm, "end": v(12.41, -32.85) * mm});
            skArc(sketch, "E176", {"start": v(11.81, -32.49) * mm, "mid": v(11.7, -32.67) * mm, "end": v(11.8, -32.85) * mm});
            skArc(sketch, "E177", {"start": v(15.26, -26.7) * mm, "mid": v(13.98, -28.63) * mm, "end": v(13.4, -30.87) * mm});
            skArc(sketch, "E178", {"start": v(18.25, -26.39) * mm, "mid": v(15.74, -28.53) * mm, "end": v(13.4, -30.87) * mm});
            skArc(sketch, "E179", {"start": v(18.25, -26.39) * mm, "mid": v(18.49, -25.89) * mm, "end": v(18.5, -25.33) * mm});
            skArc(sketch, "E180", {"start": v(15.26, -26.7) * mm, "mid": v(16.94, -26.15) * mm, "end": v(18.5, -25.33) * mm});
            skArc(sketch, "E181", {"start": v(16.29, -28.89) * mm, "mid": v(15.83, -30.76) * mm, "end": v(16.62, -32.52) * mm});
            skArc(sketch, "E182", {"start": v(14.5, -33.56) * mm, "mid": v(15.62, -33.15) * mm, "end": v(16.62, -32.52) * mm});
            skArc(sketch, "E183", {"start": v(14.5, -33.56) * mm, "mid": v(14.66, -32.18) * mm, "end": v(14.18, -30.87) * mm});
            skLineSegment(sketch, "E184", {"start": v(14.18, -30.87) * mm, "end": v(16.29, -28.89) * mm});
            skArc(sketch, "E185", {"start": v(16.91, -28.22) * mm, "mid": v(18.44, -26.87) * mm, "end": v(19.02, -24.91) * mm});
            skArc(sketch, "E186", {"start": v(16.91, -28.22) * mm, "mid": v(18.3, -31.7) * mm, "end": v(21.49, -33.65) * mm});
            skArc(sketch, "E187", {"start": v(21.49, -33.65) * mm, "mid": v(21.75, -33.01) * mm, "end": v(21.49, -32.38) * mm});
            skArc(sketch, "E188", {"start": v(18.53, -28.78) * mm, "mid": v(19.6, -30.9) * mm, "end": v(21.49, -32.38) * mm});
            skArc(sketch, "E189", {"start": v(18.53, -28.78) * mm, "mid": v(18.6, -28.01) * mm, "end": v(18.53, -27.25) * mm});
            skArc(sketch, "E190", {"start": v(18.53, -27.25) * mm, "mid": v(19.07, -26.14) * mm, "end": v(19.02, -24.91) * mm});
            skLineSegment(sketch, "E191", {"start": v(14.61, -25.93) * mm, "end": v(13.84, -25.93) * mm});
            skArc(sketch, "E192", {"start": v(22.68, -16.16) * mm, "mid": v(20.1, -17.07) * mm, "end": v(17.82, -18.6) * mm});
            skArc(sketch, "E193", {"start": v(21.4, -17.24) * mm, "mid": v(22.05, -16.7) * mm, "end": v(22.68, -16.16) * mm});
            skLineSegment(sketch, "E194", {"start": v(21.4, -17.24) * mm, "end": v(18.67, -24.15) * mm});
            skLineSegment(sketch, "E195", {"start": v(18.67, -24.15) * mm, "end": v(16.39, -24.89) * mm});
            skLineSegment(sketch, "E196", {"start": v(16.39, -24.89) * mm, "end": v(18.63, -19.67) * mm});
            skLineSegment(sketch, "E197", {"start": v(18.63, -19.67) * mm, "end": v(19.94, -19.02) * mm});
            skArc(sketch, "E198", {"start": v(19.94, -19.02) * mm, "mid": v(20.4, -18.33) * mm, "end": v(19.6, -18.17) * mm});
            skLineSegment(sketch, "E199", {"start": v(19.6, -18.17) * mm, "end": v(17.82, -19.13) * mm});
            skLineSegment(sketch, "E200", {"start": v(17.82, -19.13) * mm, "end": v(14.61, -25.93) * mm});
            skArc(sketch, "E201", {"start": v(8.97, -46.2) * mm, "mid": v(10.76, -42.54) * mm, "end": v(12.29, -38.76) * mm});
            skArc(sketch, "E202", {"start": v(17.32, -36.1) * mm, "mid": v(14.7, -37.23) * mm, "end": v(12.29, -38.76) * mm});
            skArc(sketch, "E203", {"start": v(19.65, -38.76) * mm, "mid": v(19.12, -36.88) * mm, "end": v(17.32, -36.1) * mm});
            skArc(sketch, "E204", {"start": v(14.04, -43.86) * mm, "mid": v(17.3, -41.82) * mm, "end": v(19.65, -38.76) * mm});
            skArc(sketch, "E205", {"start": v(14.04, -43.86) * mm, "mid": v(14, -43.44) * mm, "end": v(13.85, -43.05) * mm});
            skArc(sketch, "E206", {"start": v(13.85, -43.05) * mm, "mid": v(13.51, -42.88) * mm, "end": v(13.17, -43.05) * mm});
            skArc(sketch, "E207", {"start": v(13.17, -43.05) * mm, "mid": v(13.11, -43.65) * mm, "end": v(13.5, -44.13) * mm});
            skArc(sketch, "E208", {"start": v(12.88, -44.56) * mm, "mid": v(13.23, -44.4) * mm, "end": v(13.5, -44.13) * mm});
            skArc(sketch, "E209", {"start": v(12.88, -44.56) * mm, "mid": v(12.7, -44.28) * mm, "end": v(12.4, -44.13) * mm});
            skArc(sketch, "E210", {"start": v(12.4, -44.13) * mm, "mid": v(12.44, -43.86) * mm, "end": v(12.4, -43.58) * mm});
            skArc(sketch, "E211", {"start": v(12.4, -43.58) * mm, "mid": v(12.2, -43.51) * mm, "end": v(12.06, -43.66) * mm});
            skArc(sketch, "E212", {"start": v(12.06, -43.66) * mm, "mid": v(12.07, -43.9) * mm, "end": v(12.15, -44.13) * mm});
            skArc(sketch, "E213", {"start": v(12.15, -44.13) * mm, "mid": v(10.7, -45.2) * mm, "end": v(9.76, -46.74) * mm});
            skArc(sketch, "E214", {"start": v(8.97, -46.2) * mm, "mid": v(9.08, -46.9) * mm, "end": v(9.76, -46.74) * mm});
            skLineSegment(sketch, "E215", {"start": v(7.85, -48.95) * mm, "end": v(8.36, -47.68) * mm});
            skLineSegment(sketch, "E216", {"start": v(8.36, -47.68) * mm, "end": v(16.92, -42.89) * mm});
            skLineSegment(sketch, "E217", {"start": v(16.92, -42.89) * mm, "end": v(10.7, -48.49) * mm});
            skLineSegment(sketch, "E218", {"start": v(10.7, -48.49) * mm, "end": v(7.85, -48.95) * mm});
            skLineSegment(sketch, "E219", {"start": v(13.84, -25.93) * mm, "end": v(17.82, -18.6) * mm});
            skSolve(sketch);
        }
        {
            var Q0;
            Q0 = qSketchRegion(id + "F6", true);
            extrude(context, id + "F7", {"entities" : qUnion([Q0]), "operationType" : NewBodyOperationType.REMOVE, "oppositeDirection" : true, "depth" : 2.54 * mm, "offsetDistance" : 25.4 * mm});
        }
    });
